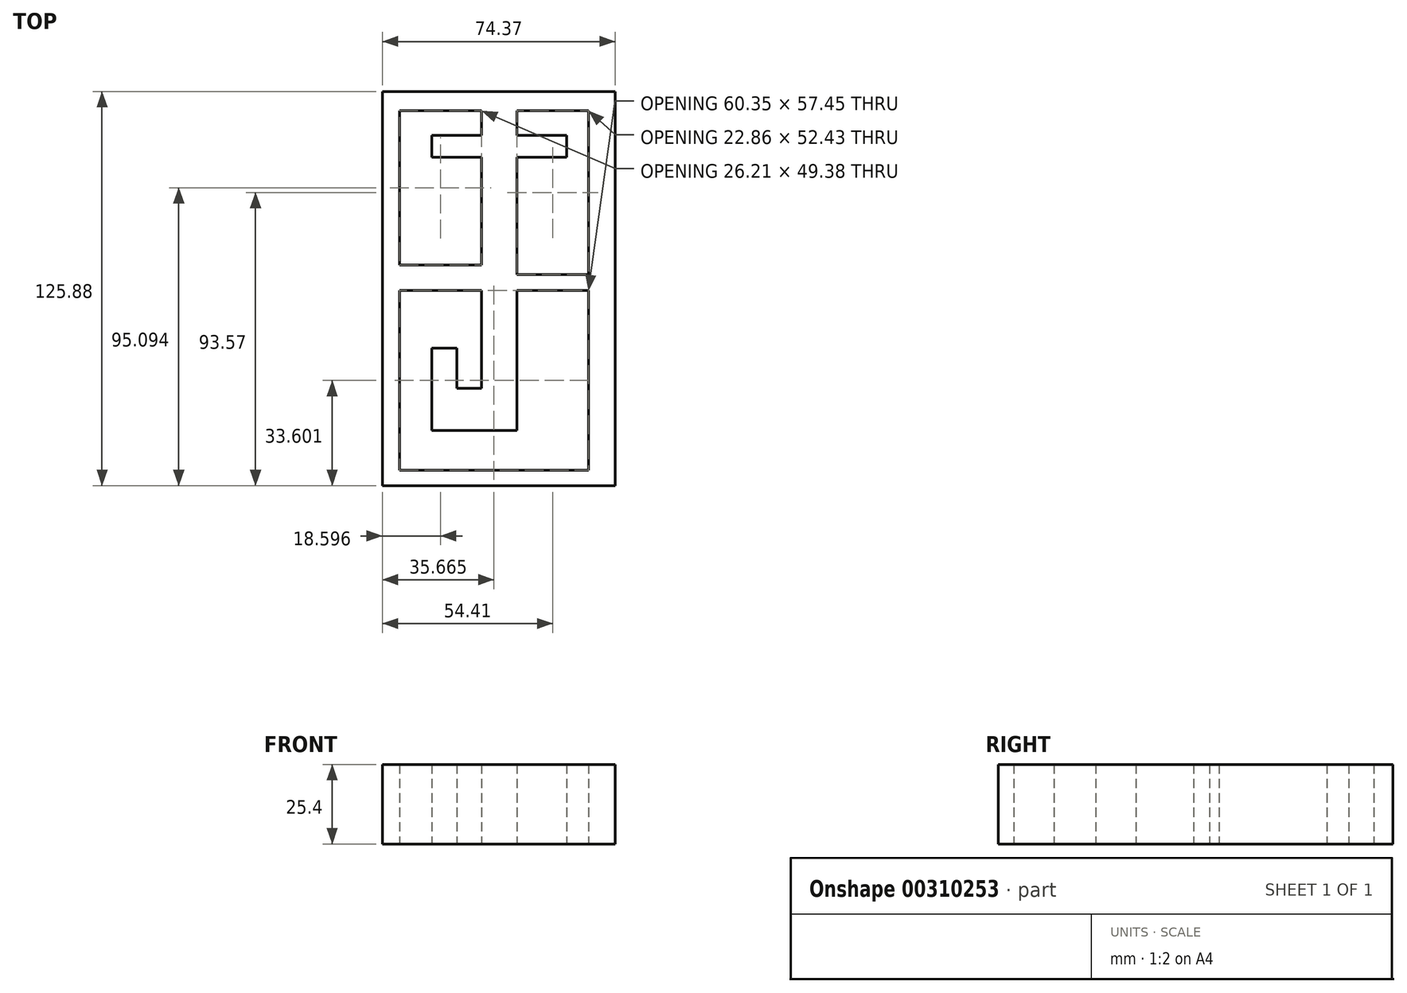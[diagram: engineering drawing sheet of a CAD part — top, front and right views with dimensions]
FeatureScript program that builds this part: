
annotation { "Feature Type Name" : "Feature", "Feature Type Description" : "" }
export const myFeature = defineFeature(function(context is Context, id is Id, definition is map)
    precondition{}
    {
        {
            var Q0;
            Q0=qCreatedBy(makeId("Top.planeOp"),FACE);
            var sketch = newSketch(context, id + "F0", { "sketchPlane" : qUnion([Q0])});
            skLineSegment(sketch, "E0.bottom", {"start": v(-53.34, 45.26) * mm, "end": v(7.01, 45.26) * mm});
            skLineSegment(sketch, "E0.top", {"start": v(-53.34, -69.65) * mm, "end": v(7.01, -69.65) * mm});
            skLineSegment(sketch, "E0.left", {"start": v(-53.34, 45.26) * mm, "end": v(-53.34, -69.65) * mm});
            skLineSegment(sketch, "E0.right", {"start": v(7.01, 45.26) * mm, "end": v(7.01, -69.65) * mm});
            skLineSegment(sketch, "E1.bottom", {"start": v(-58.83, 51.36) * mm, "end": v(15.54, 51.36) * mm});
            skLineSegment(sketch, "E1.top", {"start": v(-58.83, -74.52) * mm, "end": v(15.54, -74.52) * mm});
            skLineSegment(sketch, "E1.left", {"start": v(-58.83, 51.36) * mm, "end": v(-58.83, -74.52) * mm});
            skLineSegment(sketch, "E1.right", {"start": v(15.54, 51.36) * mm, "end": v(15.54, -74.52) * mm});
            skLineSegment(sketch, "E2", {"start": v(-27.13, 45.26) * mm, "end": v(-27.13, 37.34) * mm});
            skLineSegment(sketch, "E3", {"start": v(-27.13, 37.34) * mm, "end": v(-15.85, 37.34) * mm});
            skLineSegment(sketch, "E4", {"start": v(-15.85, 37.34) * mm, "end": v(-15.85, 45.26) * mm});
            skLineSegment(sketch, "E5", {"start": v(-15.85, 45.26) * mm, "end": v(-15.85, 37.34) * mm});
            skLineSegment(sketch, "E6", {"start": v(0, 37.34) * mm, "end": v(-15.85, 37.34) * mm});
            skLineSegment(sketch, "E7", {"start": v(-42.98, 37.34) * mm, "end": v(-27.13, 37.34) * mm});
            skLineSegment(sketch, "E8", {"start": v(-42.98, 37.34) * mm, "end": v(-42.98, 30.33) * mm});
            skLineSegment(sketch, "E9", {"start": v(-42.98, 30.33) * mm, "end": v(-27.13, 30.33) * mm});
            skLineSegment(sketch, "E10", {"start": v(-27.13, 30.33) * mm, "end": v(-27.13, -4.11) * mm});
            skLineSegment(sketch, "E11", {"start": v(-27.13, -4.11) * mm, "end": v(-53.34, -4.11) * mm});
            skLineSegment(sketch, "E12", {"start": v(-53.34, -4.11) * mm, "end": v(-53.34, -12.2) * mm});
            skLineSegment(sketch, "E13", {"start": v(-53.34, -12.2) * mm, "end": v(-27.13, -12.2) * mm});
            skLineSegment(sketch, "E14", {"start": v(-27.13, -12.2) * mm, "end": v(-27.13, -43.43) * mm});
            skLineSegment(sketch, "E15", {"start": v(-27.13, -43.43) * mm, "end": v(-35.05, -43.43) * mm});
            skLineSegment(sketch, "E16", {"start": v(-35.05, -43.43) * mm, "end": v(-35.05, -30.63) * mm});
            skLineSegment(sketch, "E17", {"start": v(-35.05, -30.63) * mm, "end": v(-42.98, -30.63) * mm});
            skLineSegment(sketch, "E18", {"start": v(-42.98, -30.63) * mm, "end": v(-42.98, -56.85) * mm});
            skLineSegment(sketch, "E19", {"start": v(-42.98, -56.85) * mm, "end": v(-15.85, -56.85) * mm});
            skLineSegment(sketch, "E20", {"start": v(-15.85, -56.85) * mm, "end": v(-15.85, -12.2) * mm});
            skLineSegment(sketch, "E21", {"start": v(-15.85, -12.2) * mm, "end": v(7.01, -12.2) * mm});
            skLineSegment(sketch, "E22", {"start": v(7.01, -12.2) * mm, "end": v(7.01, -7.16) * mm});
            skLineSegment(sketch, "E23", {"start": v(7.01, -7.16) * mm, "end": v(-15.85, -7.16) * mm});
            skLineSegment(sketch, "E24", {"start": v(-15.85, -7.16) * mm, "end": v(-15.85, 30.33) * mm});
            skLineSegment(sketch, "E25", {"start": v(-15.85, 30.33) * mm, "end": v(0, 30.33) * mm});
            skLineSegment(sketch, "E26", {"start": v(0, 30.33) * mm, "end": v(0, 37.34) * mm});
            skSolve(sketch);
        }
        {
            var Q0;
            {var subQ2=sQuery(id+"F0.wireOp",EDGE,"E0.top");Q0=makeQuery(id+"F0.imprint","IMPRINT",FACE,{"disambiguationData":[TD([[makeQuery(id+"F0.imprint","IMPRINT",EDGE,{"derivedFrom":subQ2}),-1.0]])]});}
            var Q1;
            Q1=makeQuery(id+"F0.imprint","IMPRINT",FACE,{"disambiguationData":[TD([[makeQuery(id+"F0.imprint","IMPRINT",EDGE,{"derivedFrom":sQuery(id+"F0.wireOp",EDGE,"E3")}),-1.0]])]});
            var Q2;
            {var subQ0=sQuery(id+"F0.wireOp",EDGE,"E2");Q2=makeQuery(id+"F0.imprint","IMPRINT",FACE,{"disambiguationData":[TD([[makeQuery(id+"F0.imprint","IMPRINT",EDGE,{"derivedFrom":subQ0}),1.0]])]});}
            extrude(context, id + "F1", {"entities" : qUnion([Q0, Q1, Q2]), "depth" : 25.4 * mm});
        }
    });
